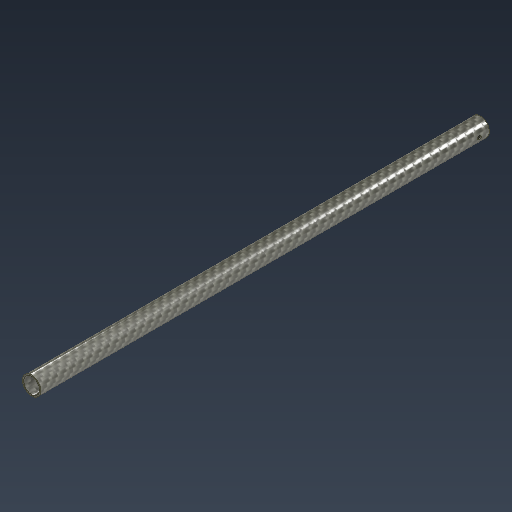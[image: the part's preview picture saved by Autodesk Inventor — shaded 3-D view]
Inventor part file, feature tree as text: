
AUTODESK INVENTOR PART (.ipt)
format: ipt  version: 2025 (Build 290162010, 162A)  size: 139,264 bytes
history: native  units: mm
features: extrude x2, sketch x1
ambient origin geometry x8: Origin, YZ Plane, XZ Plane, XY Plane, X Axis, Y Axis, Z Axis, Center Point
bodies: Solid1 (feature_tree)
feature tree (3):
  extrude  "Extrusion1"  Depth=8.75mm
  extrude  "Extrusion2"  Depth=8.75mm TaperAngle=0.0deg
  sketch  "Sketch2"  dims[d0=16.0mm d1=14.0mm d2=390.0mm d3=0.0mm d4=8.75mm d5=3.2mm d6=0.0mm d7=0.0mm]
